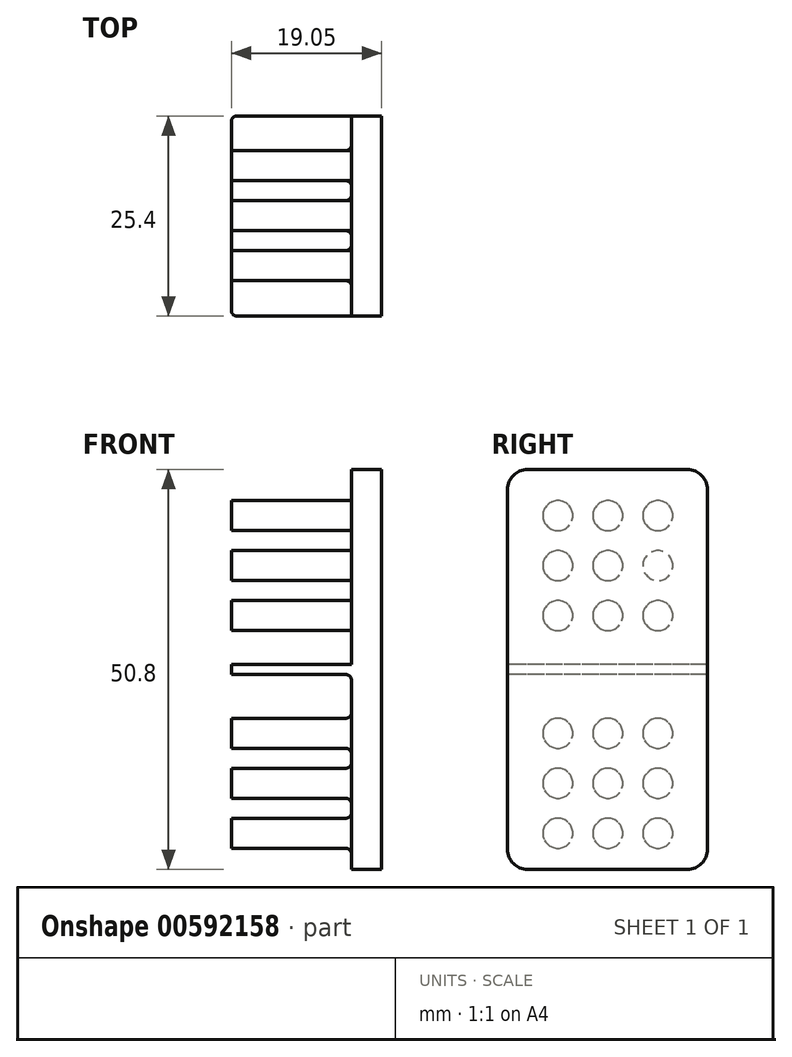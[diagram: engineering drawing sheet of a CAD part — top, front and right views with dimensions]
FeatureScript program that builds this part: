
annotation { "Feature Type Name" : "Feature", "Feature Type Description" : "" }
export const myFeature = defineFeature(function(context is Context, id is Id, definition is map)
    precondition{}
    {
        {
            var Q0;
            Q0=qCreatedBy(makeId("Right.planeOp"),FACE);
            var sketch = newSketch(context, id + "F0", { "sketchPlane" : qUnion([Q0])});
            skLineSegment(sketch, "E0.bottom", {"start": v(1.2, 0.44) * mm, "end": v(-24.2, 0.44) * mm});
            skLineSegment(sketch, "E0.top", {"start": v(1.2, -50.36) * mm, "end": v(-24.2, -50.36) * mm});
            skLineSegment(sketch, "E0.left", {"start": v(1.2, 0.44) * mm, "end": v(1.2, -50.36) * mm});
            skLineSegment(sketch, "E0.right", {"start": v(-24.2, 0.44) * mm, "end": v(-24.2, -50.36) * mm});
            skSolve(sketch);
        }
        {
            var Q0;
            Q0 = qSketchRegion(id + "F0", true);
            extrude(context, id + "F1", {"entities" : qUnion([Q0]), "depth" : 3.8 * mm, "offsetDistance" : 25.4 * mm});
        }
        {
            var Q0;
            Q0=makeQuery(id+"F1.opExtrude","CAP_FACE",FACE,{"disambiguationData":[OSD([sQuery(id+"F0.wireOp",EDGE,"E0.bottom"),sQuery(id+"F0.wireOp",EDGE,"E0.top"),sQuery(id+"F0.wireOp",EDGE,"E0.left"),sQuery(id+"F0.wireOp",EDGE,"E0.right")])],"isStart":true});
            var sketch = newSketch(context, id + "F2", { "sketchPlane" : qUnion([Q0])});
            skCircle(sketch, "E1", {"center": v(5.1, -11.77) * mm, "radius": 1.9 * mm});
            skCircle(sketch, "E2", {"center": v(11.45, -11.77) * mm, "radius": 1.9 * mm});
            skCircle(sketch, "E3", {"center": v(17.8, -11.77) * mm, "radius": 1.9 * mm});
            skCircle(sketch, "E4", {"center": v(5.1, -5.42) * mm, "radius": 1.9 * mm});
            skCircle(sketch, "E5", {"center": v(11.45, -5.42) * mm, "radius": 1.9 * mm});
            skCircle(sketch, "E6", {"center": v(17.8, -5.42) * mm, "radius": 1.9 * mm});
            skLineSegment(sketch, "E7.left", {"start": v(-1.2, -24.96) * mm, "end": v(-1.2, -24.96) * mm});
            skLineSegment(sketch, "E8.bottom", {"start": v(-1.2, -25.6) * mm, "end": v(24.2, -25.6) * mm});
            skLineSegment(sketch, "E8.top", {"start": v(-1.2, -24.33) * mm, "end": v(24.2, -24.33) * mm});
            skLineSegment(sketch, "E8.left", {"start": v(-1.2, -24.33) * mm, "end": v(-1.2, -25.6) * mm});
            skLineSegment(sketch, "E8.right", {"start": v(24.2, -24.33) * mm, "end": v(24.2, -25.6) * mm});
            skCircle(sketch, "E9", {"center": v(5.1, -18.12) * mm, "radius": 1.9 * mm});
            skCircle(sketch, "E10", {"center": v(11.45, -18.12) * mm, "radius": 1.9 * mm});
            skCircle(sketch, "E11", {"center": v(17.8, -18.12) * mm, "radius": 1.9 * mm});
            skCircle(sketch, "E12.MirrorC", {"center": v(5.1, -33.07) * mm, "radius": 1.9 * mm});
            skCircle(sketch, "E13.MirrorC", {"center": v(11.45, -33.07) * mm, "radius": 1.9 * mm});
            skCircle(sketch, "E14.MirrorC", {"center": v(17.8, -33.07) * mm, "radius": 1.9 * mm});
            skCircle(sketch, "E15.MirrorC", {"center": v(17.8, -39.42) * mm, "radius": 1.9 * mm});
            skCircle(sketch, "E16.MirrorC", {"center": v(11.45, -39.42) * mm, "radius": 1.9 * mm});
            skCircle(sketch, "E17.MirrorC", {"center": v(5.1, -39.42) * mm, "radius": 1.9 * mm});
            skCircle(sketch, "E18.MirrorC", {"center": v(17.8, -45.77) * mm, "radius": 1.9 * mm});
            skCircle(sketch, "E19.MirrorC", {"center": v(11.45, -45.77) * mm, "radius": 1.9 * mm});
            skCircle(sketch, "E20.MirrorC", {"center": v(5.1, -45.77) * mm, "radius": 1.9 * mm});
            skLineSegment(sketch, "E21", {"start": v(5.1, -5.42) * mm, "end": v(5.1, -19.1) * mm, "construction": true});
            skLineSegment(sketch, "E22", {"start": v(11.45, -5.42) * mm, "end": v(11.45, -19.56) * mm, "construction": true});
            skLineSegment(sketch, "E23", {"start": v(17.8, 11.55) * mm, "end": v(17.8, -181.14) * mm, "construction": true});
            skLineSegment(sketch, "E24", {"start": v(5.1, -18.12) * mm, "end": v(35.84, -18.12) * mm, "construction": true});
            skLineSegment(sketch, "E25", {"start": v(5.1, -5.42) * mm, "end": v(36.3, -5.42) * mm, "construction": true});
            skPoint(sketch, "E26", {"position": v(24.2, -24.96) * mm});
            skLineSegment(sketch, "E27", {"start": v(5.1, -11.77) * mm, "end": v(36.38, -11.77) * mm, "construction": true});
            skLineSegment(sketch, "E28", {"start": v(24.2, -24.96) * mm, "end": v(-1.2, -24.96) * mm, "construction": true});
            skSolve(sketch);
        }
        {
            var Q0;
            Q0 = qSketchRegion(id + "F2", true);
            extrude(context, id + "F3", {"entities" : qUnion([Q0]), "operationType" : NewBodyOperationType.ADD, "depth" : 15.24 * mm, "offsetDistance" : 25.4 * mm});
        }
        {
            var Q0;
            Q0=makeQuery(id+"F1.opExtrude","SWEPT_EDGE",EDGE,{"disambiguationData":[OSD([sQuery(id+"F0.wireOp",EDGE,"E0.top"),sQuery(id+"F0.wireOp",EDGE,"E0.right")])]});
            var Q1;
            Q1=makeQuery(id+"F1.opExtrude","SWEPT_EDGE",EDGE,{"disambiguationData":[OSD([sQuery(id+"F0.wireOp",EDGE,"E0.bottom"),sQuery(id+"F0.wireOp",EDGE,"E0.right")])]});
            var Q2;
            Q2=makeQuery(id+"F1.opExtrude","SWEPT_EDGE",EDGE,{"disambiguationData":[OSD([sQuery(id+"F0.wireOp",EDGE,"E0.top"),sQuery(id+"F0.wireOp",EDGE,"E0.left")])]});
            var Q3;
            Q3=makeQuery(id+"F1.opExtrude","SWEPT_EDGE",EDGE,{"disambiguationData":[OSD([sQuery(id+"F0.wireOp",EDGE,"E0.bottom"),sQuery(id+"F0.wireOp",EDGE,"E0.left")])]});
            fillet(context, id + "F4", {"entities" : qUnion([Q0, Q1, Q2, Q3]), "radius" : 2.54 * mm, "tangentPropagation" : true, "allowEdgeOverflow" : false});
        }
        {
            var Q0;
            Q0=makeQuery(id+"F3.opExtrude","CAP_EDGE",EDGE,{"disambiguationData":[OSD([sQuery(id+"F2.wireOp",EDGE,"E8.left")])],"isStart":false});
            var Q1;
            Q1=makeQuery(id+"F3.opExtrude","CAP_EDGE",EDGE,{"disambiguationData":[OSD([sQuery(id+"F2.wireOp",EDGE,"E8.right")])],"isStart":false});
            fillet(context, id + "F5", {"entities" : qUnion([Q0, Q1]), "radius" : 0.64 * mm, "tangentPropagation" : true, "allowEdgeOverflow" : false});
        }
        {
            var Q0;
            Q0=makeQuery(id+"F3.opExtrude","CAP_EDGE",EDGE,{"disambiguationData":[OSD([sQuery(id+"F2.wireOp",EDGE,"E9")])],"isStart":true});
            var Q1;
            Q1=makeQuery(id+"F3.opExtrude","CAP_EDGE",EDGE,{"disambiguationData":[OSD([sQuery(id+"F2.wireOp",EDGE,"E1")])],"isStart":true});
            var Q2;
            Q2=makeQuery(id+"F3.opExtrude","CAP_EDGE",EDGE,{"disambiguationData":[OSD([sQuery(id+"F2.wireOp",EDGE,"E4")])],"isStart":true});
            var Q3;
            Q3=makeQuery(id+"F3.opExtrude","CAP_EDGE",EDGE,{"disambiguationData":[OSD([sQuery(id+"F2.wireOp",EDGE,"E5")])],"isStart":true});
            var Q4;
            Q4=makeQuery(id+"F3.opExtrude","CAP_EDGE",EDGE,{"disambiguationData":[OSD([sQuery(id+"F2.wireOp",EDGE,"E2")])],"isStart":true});
            var Q5;
            Q5=makeQuery(id+"F3.opExtrude","CAP_EDGE",EDGE,{"disambiguationData":[OSD([sQuery(id+"F2.wireOp",EDGE,"E3")])],"isStart":true});
            var Q6;
            Q6=makeQuery(id+"F3.opExtrude","CAP_EDGE",EDGE,{"disambiguationData":[OSD([sQuery(id+"F2.wireOp",EDGE,"E6")])],"isStart":true});
            var Q7;
            Q7=makeQuery(id+"F3.opExtrude","CAP_EDGE",EDGE,{"disambiguationData":[OSD([sQuery(id+"F2.wireOp",EDGE,"E12.MirrorC")])],"isStart":true});
            var Q8;
            Q8=makeQuery(id+"F3.opExtrude","CAP_EDGE",EDGE,{"disambiguationData":[OSD([sQuery(id+"F2.wireOp",EDGE,"E10")])],"isStart":true});
            var Q9;
            Q9=makeQuery(id+"F3.opExtrude","CAP_EDGE",EDGE,{"disambiguationData":[OSD([sQuery(id+"F2.wireOp",EDGE,"E11")])],"isStart":true});
            var Q10;
            Q10=makeQuery(id+"F3.opExtrude","CAP_EDGE",EDGE,{"disambiguationData":[OSD([sQuery(id+"F2.wireOp",EDGE,"E13.MirrorC")])],"isStart":true});
            var Q11;
            Q11=makeQuery(id+"F3.opExtrude","CAP_EDGE",EDGE,{"disambiguationData":[OSD([sQuery(id+"F2.wireOp",EDGE,"E14.MirrorC")])],"isStart":true});
            var Q12;
            Q12=makeQuery(id+"F3.opExtrude","CAP_EDGE",EDGE,{"disambiguationData":[OSD([sQuery(id+"F2.wireOp",EDGE,"E17.MirrorC")])],"isStart":true});
            var Q13;
            Q13=makeQuery(id+"F3.opExtrude","CAP_EDGE",EDGE,{"disambiguationData":[OSD([sQuery(id+"F2.wireOp",EDGE,"E16.MirrorC")])],"isStart":true});
            var Q14;
            Q14=makeQuery(id+"F3.opExtrude","CAP_EDGE",EDGE,{"disambiguationData":[OSD([sQuery(id+"F2.wireOp",EDGE,"E15.MirrorC")])],"isStart":true});
            var Q15;
            Q15=makeQuery(id+"F3.opExtrude","CAP_EDGE",EDGE,{"disambiguationData":[OSD([sQuery(id+"F2.wireOp",EDGE,"E18.MirrorC")])],"isStart":true});
            var Q16;
            Q16=makeQuery(id+"F3.opExtrude","CAP_EDGE",EDGE,{"disambiguationData":[OSD([sQuery(id+"F2.wireOp",EDGE,"E19.MirrorC")])],"isStart":true});
            var Q17;
            Q17=makeQuery(id+"F3.opExtrude","CAP_EDGE",EDGE,{"disambiguationData":[OSD([sQuery(id+"F2.wireOp",EDGE,"E20.MirrorC")])],"isStart":true});
            var Q18;
            Q18=makeQuery(id+"F3.opExtrude","CAP_EDGE",EDGE,{"disambiguationData":[OSD([sQuery(id+"F2.wireOp",EDGE,"E8.top")])],"isStart":true});
            var Q19;
            Q19=makeQuery(id+"F3.opExtrude","CAP_EDGE",EDGE,{"disambiguationData":[OSD([sQuery(id+"F2.wireOp",EDGE,"E8.bottom")])],"isStart":true});
            fillet(context, id + "F6", {"entities" : qUnion([Q0, Q1, Q2, Q3, Q4, Q5, Q6, Q7, Q8, Q9, Q10, Q11, Q12, Q13, Q14, Q15, Q16, Q17, Q18, Q19]), "radius" : 0.76 * mm, "tangentPropagation" : true, "allowEdgeOverflow" : false});
        }
    });
